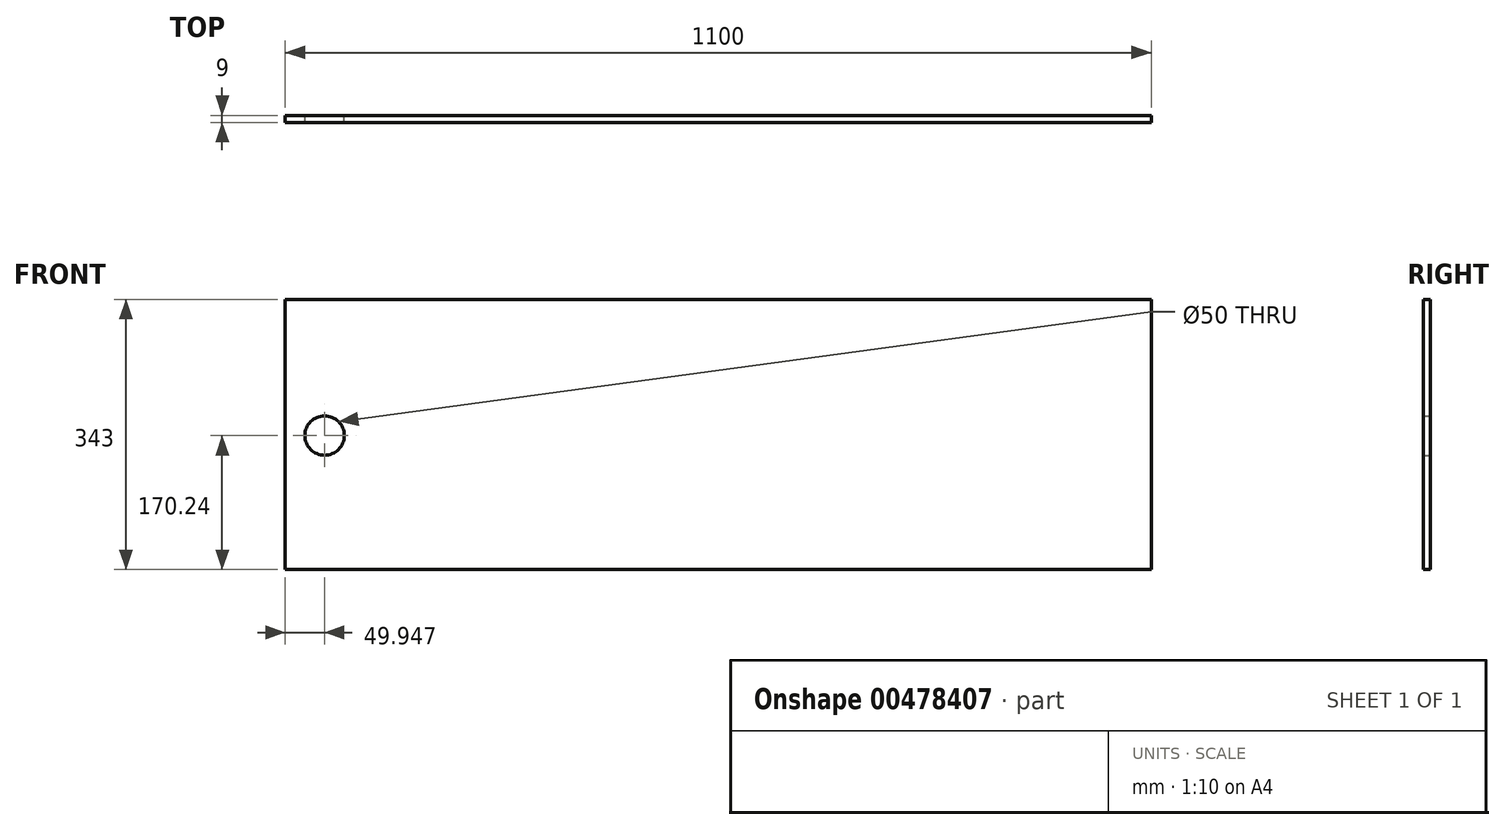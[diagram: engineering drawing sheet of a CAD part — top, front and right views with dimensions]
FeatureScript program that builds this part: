
annotation { "Feature Type Name" : "Feature", "Feature Type Description" : "" }
export const myFeature = defineFeature(function(context is Context, id is Id, definition is map)
    precondition{}
    {
        {
            var Q0;
            Q0=qCreatedBy(makeId("Front.planeOp"),FACE);
            var sketch = newSketch(context, id + "F0", { "sketchPlane" : qUnion([Q0])});
            skLineSegment(sketch, "E0.bottom", {"start": v(-286.9, 172.76) * mm, "end": v(813.1, 172.76) * mm});
            skLineSegment(sketch, "E0.top", {"start": v(-286.9, -170.24) * mm, "end": v(813.1, -170.24) * mm});
            skLineSegment(sketch, "E0.left", {"start": v(-286.9, 172.76) * mm, "end": v(-286.9, -170.24) * mm});
            skLineSegment(sketch, "E0.right", {"start": v(813.1, 172.76) * mm, "end": v(813.1, -170.24) * mm});
            skLineSegment(sketch, "E1", {"start": v(-286.9, 0) * mm, "end": v(813.1, 0) * mm, "construction": true});
            skLineSegment(sketch, "E2", {"start": v(-286.9, 172.76) * mm, "end": v(-187.75, -170.24) * mm, "construction": true});
            skCircle(sketch, "E3", {"center": v(-236.96, 0) * mm, "radius": 25 * mm});
            skSolve(sketch);
        }
        {
            var Q0;
            Q0=makeQuery(id+"F0.imprint","IMPRINT",FACE,{"disambiguationData":[TD([[makeQuery(id+"F0.imprint","IMPRINT",EDGE,{"derivedFrom":sQuery(id+"F0.wireOp",EDGE,"E0.bottom")}),-1.0]])]});
            extrude(context, id + "F1", {"entities" : qUnion([Q0]), "depth" : 9 * mm});
        }
    });
